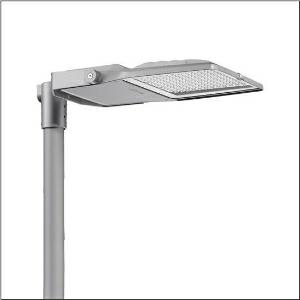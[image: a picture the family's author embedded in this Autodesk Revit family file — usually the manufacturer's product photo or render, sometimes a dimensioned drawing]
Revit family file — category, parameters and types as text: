
# Revit family: floodlight_fl_21_iq_midi___pl43_5xa7782f4a3a_c232
name_source: partatom
category: Lighting Fixtures
units: mm (PartAtom-declared; Revit-internal decimal feet)

## family parameters
Cut with Voids When Loaded = No
Host = Face
Light Source = No
Part Type = Normal
Room Calculation Point = No
Round Connector Dimension = Use Diameter
Shared = No

## types (1)
- --- (1 x LED, 38290 lm, 270.2 W, 4000K)
    Apparent Load = 270 VA
    CIE Flux Codes = 27 78 99 100 100
    Color Rendering = 70
    Color Temperature = 4000K
    Default Elevation = 1800 mm
    Description = Floodlight FL 21 iQ midi, floodlight, primary light control with lens, of PMMA, primary optical cover: protective disc, of toughened safety glass, transparent, light distribution: PL43, light emission: direct distribution, installation type: surface-mounted, LED, High Power LED, rated luminous flux: 38.290lm, luminous efficacy: 142lm/W, light colour: 740, colour temperature: 4000K, control gear: iQ Street-Remote/DALI, control: optimised constant luminous flux control (CLO 2.0), Desk-Remote (wireless, voltage-free reading and setting of iQ features in the workshop via application-optimized NFC function/RFID function), Smart-Wire, Night-Set, Temp-Guard, Auto-Match, Street-Remote, with terminal, 6-pole, mains connection: 220..240V, AC, 50/60Hz, start of lifetime: 270W, end of service life: 287W, reduction: 118W, luminaire housing, of diecast aluminium, powder-coated, Siteco® metallic grey (DB 702S), corrosivity category C5 mid according to DIN EN ISO 12944, suitable for swimming pools, chlorine-resistant, sealing non-destructively replaceable, please order mast flange separately, mast bracket, of steel, galvanised, powder-coated, Siteco® metallic grey (DB 702S), protection rating (complete): IP66, insulation class (complete): insulation class II (safety insulation), certification: CE, ENEC, VDE, protection symbol: D, impact resistance: IK08, permissible operating ambient temperature: -40..+40°C, permissible operating ambient temperature for outdoor applications: -40..+50°C, standard: DIN EN 12944, LABS conformity tested according to VDMA 24364:2018-05, packaging unit: 1 piece

Light Distribution: PL43
    Height = 76 mm
    Lamp = 1 x LED
    Lamp Light Flux = 38290 lm
    Lamp Power = 270.2 W
    Lamp count = 1
    Length = 657 mm
    Luminous efficacy = 142 lm/W
    Manufacturer = Siteco
    ModVariant = No
    Model = 5XA7782F4A3A
    Number of Poles = 1
    OnlyDefault = Yes
    Power Factor = 1
    Product Name = Floodlight FL 21 iQ midi | PL43
    Product group = floodlight | pylon annexe
    ProductGroupID = 6200
    Protection Class = Protection class II
    Protection Degree = IP 66
    RLX_Detail_Level = 1
    RLX_Emergency_Light_Flux = 0 lm
    RLX_Emergency_Type = 0
    RLX_Emergency_Type_DB = No
    RlxData = <blob elided: 153541 chars, md5=32ee1fbd>
    Socket = socket
    Standby Power = 0 W
    System Light Flux = 38290 lm
    System Power = 270 W
    Type Comments = factory setting: luminous flux: 100 % | dim-lin: 254 | 620 mA
    Type Image = l_1007123.jpg
    URL = http://relux.com
    VarID = @adj_104584
    Voltage = 0 V
    Weight = 0.00 kg
    Width = 442 mm

## geometry (parser evidence)
native form markers: Blend x4, Sweep x13
no freeform markers — native parametric forms only
